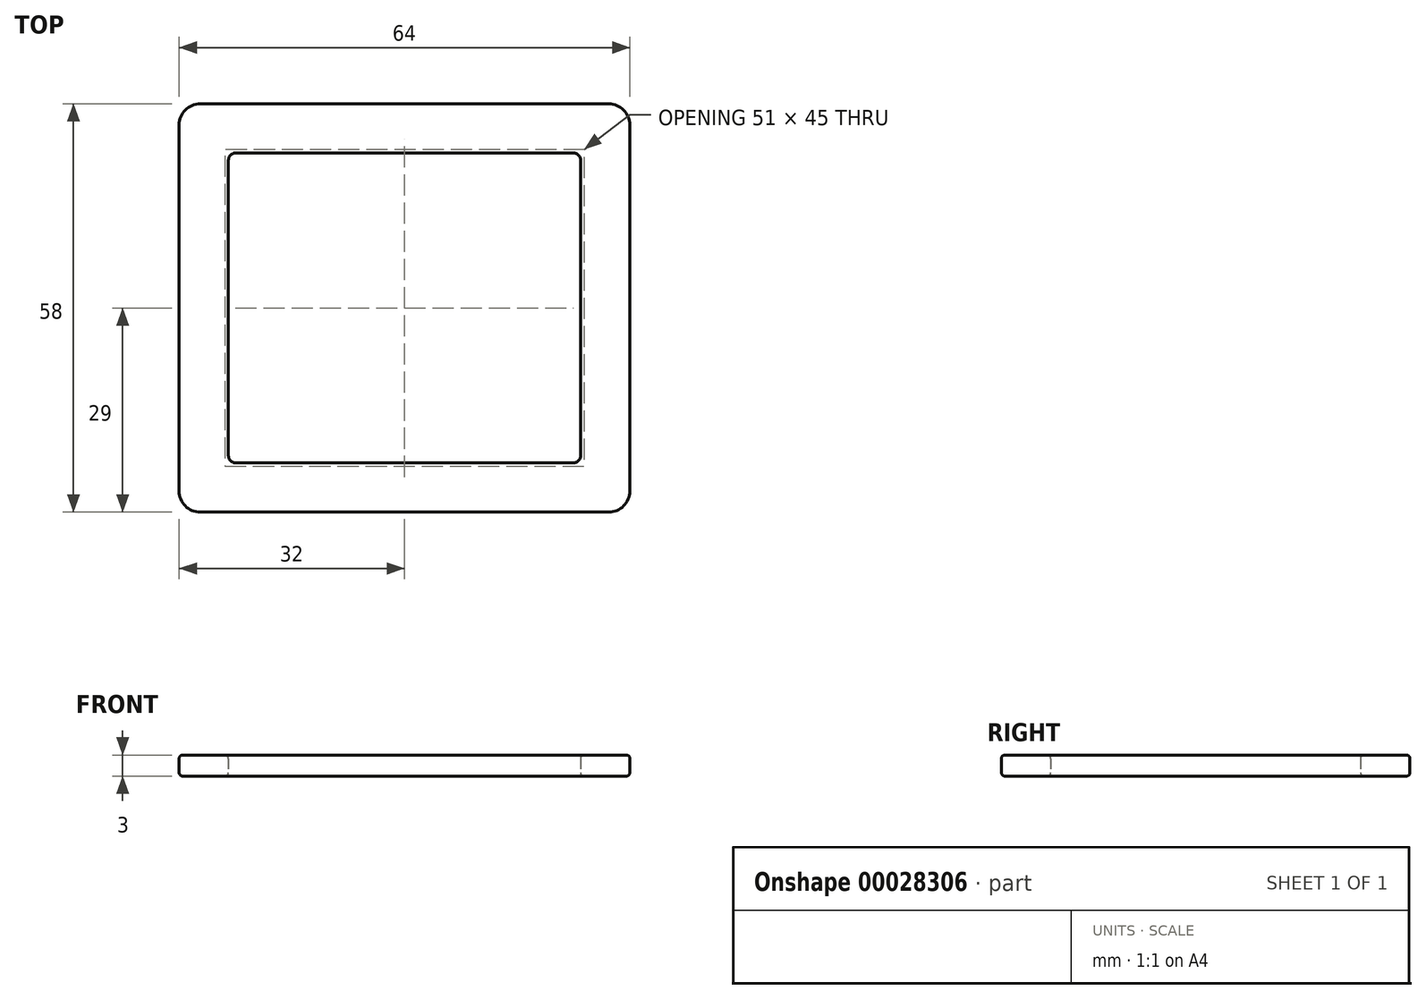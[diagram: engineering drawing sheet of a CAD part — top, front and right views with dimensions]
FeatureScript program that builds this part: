
annotation { "Feature Type Name" : "Feature", "Feature Type Description" : "" }
export const myFeature = defineFeature(function(context is Context, id is Id, definition is map)
    precondition{}
    {
        {
            var Q0;
            Q0=qCreatedBy(makeId("Top.planeOp"),FACE);
            var sketch = newSketch(context, id + "F0", { "sketchPlane" : qUnion([Q0])});
            skLineSegment(sketch, "E0.bottom", {"start": v(1, 0) * mm, "end": v(49, 0) * mm});
            skLineSegment(sketch, "E0.top", {"start": v(1, 44) * mm, "end": v(49, 44) * mm});
            skLineSegment(sketch, "E0.left", {"start": v(0, 1) * mm, "end": v(0, 43) * mm});
            skLineSegment(sketch, "E0.right", {"start": v(50, 1) * mm, "end": v(50, 43) * mm});
            skLineSegment(sketch, "E1.0", {"start": v(-7, -4) * mm, "end": v(-7, 48) * mm});
            skLineSegment(sketch, "E1.1", {"start": v(-4, -7) * mm, "end": v(54, -7) * mm});
            skLineSegment(sketch, "E1.2", {"start": v(57, -4) * mm, "end": v(57, 48) * mm});
            skLineSegment(sketch, "E1.3", {"start": v(-4, 51) * mm, "end": v(54, 51) * mm});
            skPoint(sketch, "E2.visualSharp", {"position": v(-7, 51) * mm});
            skArc(sketch, "E2.filletArc", {"start": v(-4, 51) * mm, "mid": v(-6.12, 50.12) * mm, "end": v(-7, 48) * mm});
            skPoint(sketch, "E3.visualSharp", {"position": v(57, 51) * mm});
            skArc(sketch, "E3.filletArc", {"start": v(57, 48) * mm, "mid": v(56.12, 50.12) * mm, "end": v(54, 51) * mm});
            skPoint(sketch, "E4.visualSharp", {"position": v(57, -7) * mm});
            skArc(sketch, "E4.filletArc", {"start": v(54, -7) * mm, "mid": v(56.12, -6.12) * mm, "end": v(57, -4) * mm});
            skPoint(sketch, "E5.visualSharp", {"position": v(-7, -7) * mm});
            skArc(sketch, "E5.filletArc", {"start": v(-7, -4) * mm, "mid": v(-6.12, -6.12) * mm, "end": v(-4, -7) * mm});
            skPoint(sketch, "E6.visualSharp", {"position": v(0, 44) * mm});
            skArc(sketch, "E6.filletArc", {"start": v(1, 44) * mm, "mid": v(0.3, 43.7) * mm, "end": v(0, 43) * mm});
            skPoint(sketch, "E7.visualSharp", {"position": v(50, 44) * mm});
            skArc(sketch, "E7.filletArc", {"start": v(50, 43) * mm, "mid": v(49.7, 43.7) * mm, "end": v(49, 44) * mm});
            skPoint(sketch, "E8.visualSharp", {"position": v(50, 0) * mm});
            skArc(sketch, "E8.filletArc", {"start": v(49, 0) * mm, "mid": v(49.7, 0.3) * mm, "end": v(50, 1) * mm});
            skPoint(sketch, "E9.visualSharp", {"position": v(0, 0) * mm});
            skArc(sketch, "E9.filletArc", {"start": v(0, 1) * mm, "mid": v(0.3, 0.3) * mm, "end": v(1, 0) * mm});
            skSolve(sketch);
        }
        {
            var Q0;
            Q0=makeQuery(id+"F0.imprint","IMPRINT",FACE,{"disambiguationData":[TD([[makeQuery(id+"F0.imprint","IMPRINT",EDGE,{"derivedFrom":sQuery(id+"F0.wireOp",EDGE,"E0.bottom")}),-1.0]])]});
            extrude(context, id + "F1", {"entities" : qUnion([Q0]), "depth" : 3 * mm});
        }
        {
            var Q0;
            Q0=makeQuery(id+"F1.opExtrude","CAP_EDGE",EDGE,{"disambiguationData":[OSD([sQuery(id+"F0.wireOp",EDGE,"E0.top")])],"isStart":false});
            var Q1;
            Q1=makeQuery(id+"F1.opExtrude","CAP_EDGE",EDGE,{"disambiguationData":[OSD([sQuery(id+"F0.wireOp",EDGE,"E1.3")])],"isStart":false});
            var Q2;
            Q2=makeQuery(id+"F1.opExtrude","CAP_EDGE",EDGE,{"disambiguationData":[OSD([sQuery(id+"F0.wireOp",EDGE,"E0.top")])],"isStart":true});
            var Q3;
            Q3=makeQuery(id+"F1.opExtrude","CAP_EDGE",EDGE,{"disambiguationData":[OSD([sQuery(id+"F0.wireOp",EDGE,"E1.1")])],"isStart":true});
            fillet(context, id + "F2", {"entities" : qUnion([Q0, Q1, Q2, Q3]), "radius" : 0.5 * mm, "tangentPropagation" : true, "allowEdgeOverflow" : false});
        }
    });
